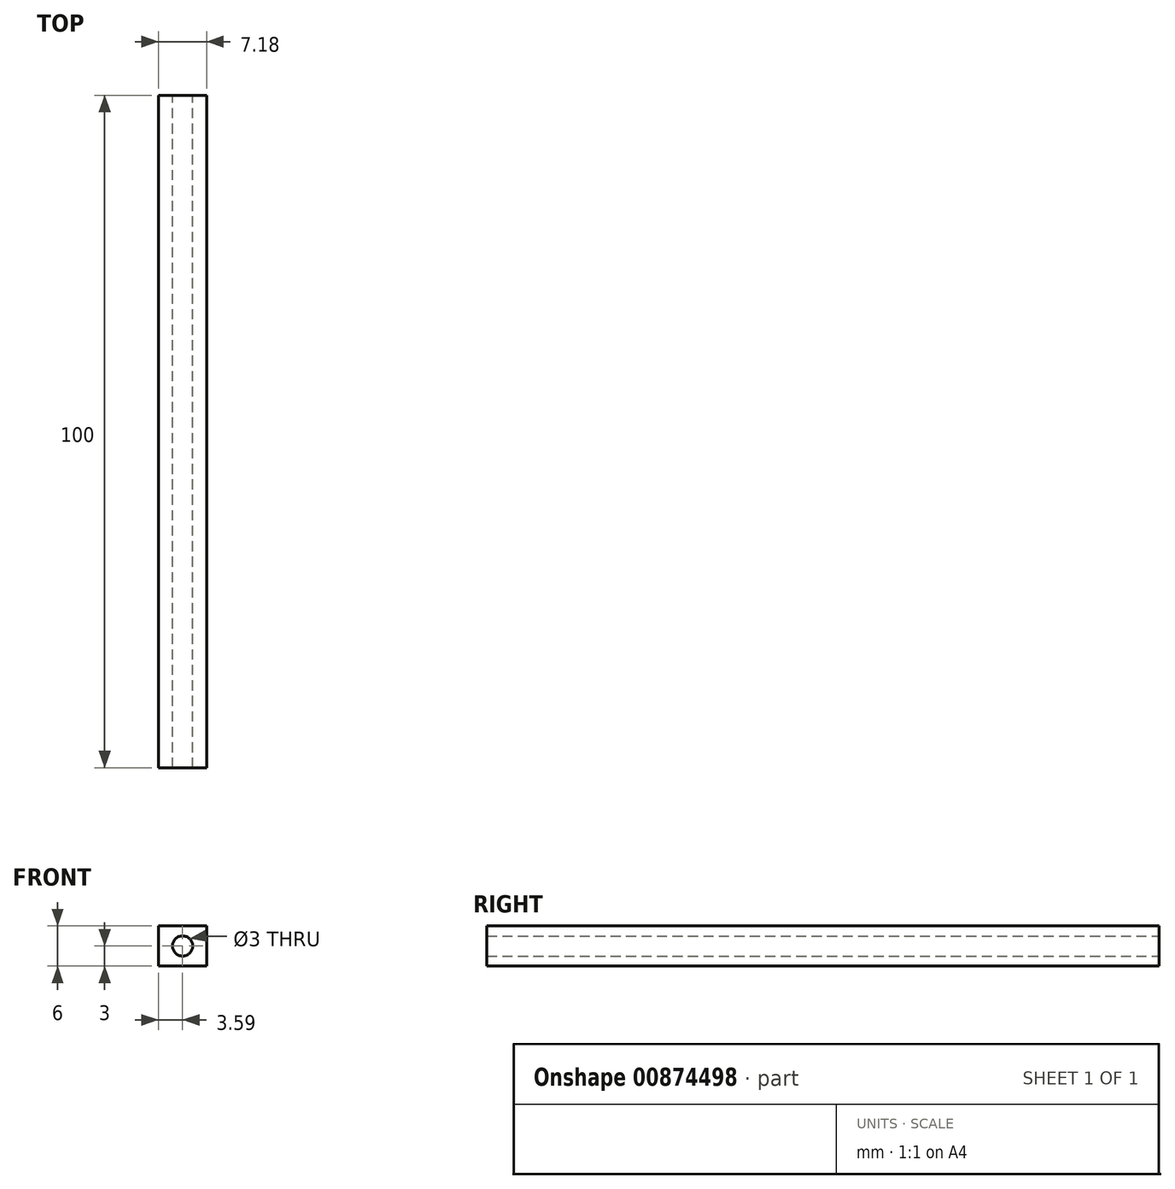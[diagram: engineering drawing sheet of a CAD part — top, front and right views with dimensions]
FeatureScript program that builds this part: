
annotation { "Feature Type Name" : "Feature", "Feature Type Description" : "" }
export const myFeature = defineFeature(function(context is Context, id is Id, definition is map)
    precondition{}
    {
        {
            var Q0;
            Q0=qCreatedBy(makeId("Front.planeOp"),FACE);
            var sketch = newSketch(context, id + "F0", { "sketchPlane" : qUnion([Q0])});
            skLineSegment(sketch, "E0.bottom", {"start": v(3.59, -3) * mm, "end": v(-3.59, -3) * mm});
            skLineSegment(sketch, "E0.top", {"start": v(3.59, 3) * mm, "end": v(-3.59, 3) * mm});
            skLineSegment(sketch, "E0.left", {"start": v(3.59, -3) * mm, "end": v(3.59, 3) * mm});
            skLineSegment(sketch, "E0.right", {"start": v(-3.59, -3) * mm, "end": v(-3.59, 3) * mm});
            skPoint(sketch, "E0.middle", {"position": v(0, 0) * mm});
            skCircle(sketch, "E1", {"center": v(0, 0) * mm, "radius": 1.5 * mm});
            skSolve(sketch);
        }
        {
            var Q0;
            Q0 = qSketchRegion(id + "F0", true);
            extrude(context, id + "F1", {"entities" : qUnion([Q0]), "depth" : 100 * mm, "offsetDistance" : 25 * mm});
        }
    });
